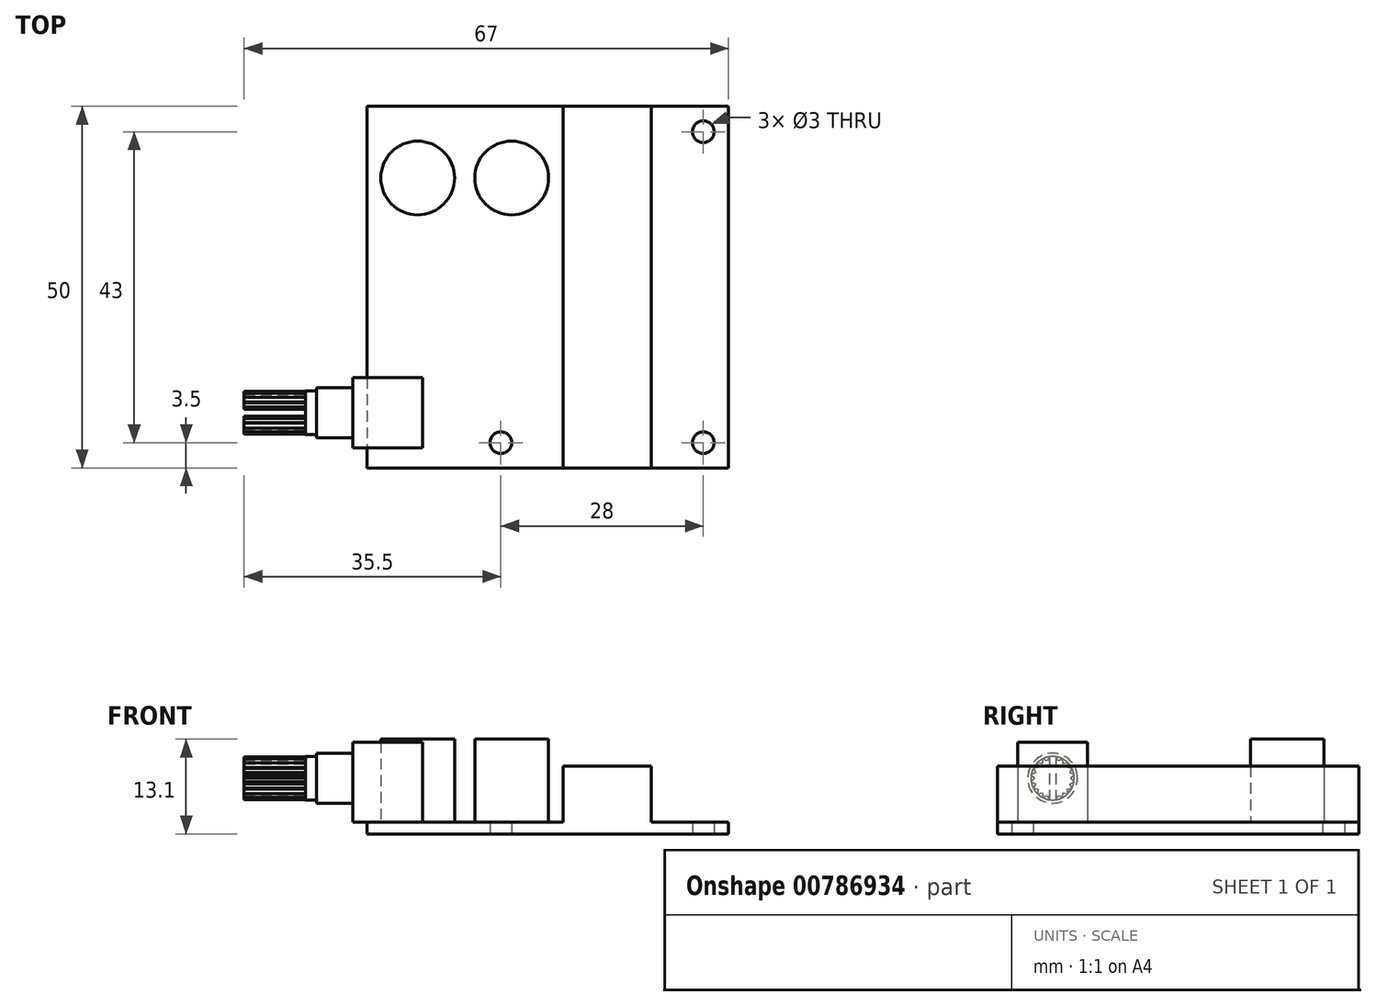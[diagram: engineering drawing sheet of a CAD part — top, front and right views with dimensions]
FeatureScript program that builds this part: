
annotation { "Feature Type Name" : "Feature", "Feature Type Description" : "" }
export const myFeature = defineFeature(function(context is Context, id is Id, definition is map)
    precondition{}
    {
        {
            var Q0;
            Q0=qCreatedBy(makeId("Top.planeOp"),FACE);
            var sketch = newSketch(context, id + "F0", { "sketchPlane" : qUnion([Q0])});
            skLineSegment(sketch, "E0.bottom", {"start": v(-25, 25) * mm, "end": v(25, 25) * mm});
            skLineSegment(sketch, "E0.top", {"start": v(-25, -25) * mm, "end": v(25, -25) * mm});
            skLineSegment(sketch, "E0.left", {"start": v(-25, 25) * mm, "end": v(-25, -25) * mm});
            skLineSegment(sketch, "E0.right", {"start": v(25, 25) * mm, "end": v(25, -25) * mm});
            skCircle(sketch, "E1", {"center": v(21.5, 21.5) * mm, "radius": 1.5 * mm});
            skCircle(sketch, "E2", {"center": v(21.5, -21.5) * mm, "radius": 1.5 * mm});
            skCircle(sketch, "E3", {"center": v(-6.5, -21.5) * mm, "radius": 1.5 * mm});
            skSolve(sketch);
        }
        {
            var Q0;
            Q0=makeQuery(id+"F0.imprint","IMPRINT",FACE,{"disambiguationData":[TD([[makeQuery(id+"F0.imprint","IMPRINT",EDGE,{"derivedFrom":sQuery(id+"F0.wireOp",EDGE,"E0.bottom")}),-1.0]])]});
            extrude(context, id + "F1", {"entities" : qUnion([Q0]), "depth" : 1.6 * mm, "offsetDistance" : 25 * mm});
        }
        {
            var Q0;
            Q0=makeQuery(id+"F1.opExtrude","CAP_FACE",FACE,{"disambiguationData":[OSD([sQuery(id+"F0.wireOp",EDGE,"E0.bottom"),sQuery(id+"F0.wireOp",EDGE,"E0.top"),sQuery(id+"F0.wireOp",EDGE,"E0.left"),sQuery(id+"F0.wireOp",EDGE,"E0.right"),sQuery(id+"F0.wireOp",EDGE,"E1"),sQuery(id+"F0.wireOp",EDGE,"E2"),sQuery(id+"F0.wireOp",EDGE,"E3")])],"isStart":false});
            var sketch = newSketch(context, id + "F2", { "sketchPlane" : qUnion([Q0])});
            skLineSegment(sketch, "E4.bottom", {"start": v(2.1, 25) * mm, "end": v(14.3, 25) * mm});
            skLineSegment(sketch, "E4.top", {"start": v(2.1, -25) * mm, "end": v(14.3, -25) * mm});
            skLineSegment(sketch, "E4.left", {"start": v(2.1, 25) * mm, "end": v(2.1, -25) * mm});
            skLineSegment(sketch, "E4.right", {"start": v(14.3, 25) * mm, "end": v(14.3, -25) * mm});
            skSolve(sketch);
        }
        {
            var Q0;
            Q0 = qSketchRegion(id + "F2", true);
            extrude(context, id + "F3", {"entities" : qUnion([Q0]), "operationType" : NewBodyOperationType.ADD, "depth" : (9.37 - 1.6) * mm, "offsetDistance" : 25 * mm});
        }
        {
            var Q0;
            {var subQ0=sQuery(id+"F0.wireOp",EDGE,"E0.left");var subQ1=sQuery(id+"F0.wireOp",EDGE,"E3");var subQ2=sQuery(id+"F0.wireOp",EDGE,"E0.top");var subQ3=sQuery(id+"F0.wireOp",EDGE,"E0.bottom");Q0=makeQuery(id+"F3.boolean.opBoolean","SPLIT",FACE,{"disambiguationData":[TD([makeQuery(id+"F1.opExtrude","SWEPT_FACE",FACE,{"disambiguationData":[OSD([subQ0])]})])],"derivedFrom":makeQuery(id+"F1.opExtrude","CAP_FACE",FACE,{"disambiguationData":[OSD([subQ3,subQ2,subQ0,sQuery(id+"F0.wireOp",EDGE,"E0.right"),sQuery(id+"F0.wireOp",EDGE,"E1"),sQuery(id+"F0.wireOp",EDGE,"E2"),subQ1])],"isStart":false})});}
            var sketch = newSketch(context, id + "F4", { "sketchPlane" : qUnion([Q0])});
            skCircle(sketch, "E5", {"center": v(-18, 15.1) * mm, "radius": 5.1 * mm});
            skCircle(sketch, "E6", {"center": v(-5, 15.1) * mm, "radius": 5.1 * mm});
            skSolve(sketch);
        }
        {
            var Q0;
            Q0 = qSketchRegion(id + "F4", true);
            extrude(context, id + "F5", {"entities" : qUnion([Q0]), "operationType" : NewBodyOperationType.ADD, "depth" : (13.1 - 1.6) * mm, "offsetDistance" : 25 * mm});
        }
        {
            var Q0;
            {var subQ0=sQuery(id+"F0.wireOp",EDGE,"E0.left");var subQ1=sQuery(id+"F0.wireOp",EDGE,"E3");var subQ2=sQuery(id+"F0.wireOp",EDGE,"E0.top");var subQ3=sQuery(id+"F0.wireOp",EDGE,"E0.bottom");Q0=makeQuery(id+"F3.boolean.opBoolean","SPLIT",FACE,{"disambiguationData":[TD([makeQuery(id+"F1.opExtrude","SWEPT_FACE",FACE,{"disambiguationData":[OSD([subQ0])]})])],"derivedFrom":makeQuery(id+"F1.opExtrude","CAP_FACE",FACE,{"disambiguationData":[OSD([subQ3,subQ2,subQ0,sQuery(id+"F0.wireOp",EDGE,"E0.right"),sQuery(id+"F0.wireOp",EDGE,"E1"),sQuery(id+"F0.wireOp",EDGE,"E2"),subQ1])],"isStart":false})});}
            var sketch = newSketch(context, id + "F6", { "sketchPlane" : qUnion([Q0])});
            skLineSegment(sketch, "E7.bottom", {"start": v(-27, -12.5) * mm, "end": v(-17.3, -12.5) * mm});
            skLineSegment(sketch, "E7.top", {"start": v(-27, -22.2) * mm, "end": v(-17.3, -22.2) * mm});
            skLineSegment(sketch, "E7.left", {"start": v(-27, -12.5) * mm, "end": v(-27, -22.2) * mm});
            skLineSegment(sketch, "E7.right", {"start": v(-17.3, -12.5) * mm, "end": v(-17.3, -22.2) * mm});
            skSolve(sketch);
        }
        {
            var Q0;
            Q0 = qSketchRegion(id + "F6", true);
            extrude(context, id + "F7", {"entities" : qUnion([Q0]), "operationType" : NewBodyOperationType.ADD, "depth" : 11.1 * mm, "offsetDistance" : 25 * mm});
        }
        {
            var Q0;
            Q0=makeQuery(id+"F7.opExtrude","SWEPT_FACE",FACE,{"disambiguationData":[OSD([sQuery(id+"F6.wireOp",EDGE,"E7.left")])]});
            var sketch = newSketch(context, id + "F8", { "sketchPlane" : qUnion([Q0])});
            skCircle(sketch, "E8", {"center": v(17.35, 7.7) * mm, "radius": 3.45 * mm});
            skSolve(sketch);
        }
        {
            var Q0;
            Q0 = qSketchRegion(id + "F8", true);
            extrude(context, id + "F9", {"entities" : qUnion([Q0]), "operationType" : NewBodyOperationType.ADD, "depth" : 5 * mm, "offsetDistance" : 25 * mm});
        }
        {
            var Q0;
            Q0=makeQuery(id+"F9.opExtrude","CAP_FACE",FACE,{"disambiguationData":[OSD([sQuery(id+"F8.wireOp",EDGE,"E8")])],"isStart":false});
            var sketch = newSketch(context, id + "F10", { "sketchPlane" : qUnion([Q0])});
            skCircle(sketch, "E9", {"center": v(17.35, 7.7) * mm, "radius": 3 * mm});
            skSolve(sketch);
        }
        {
            var Q0;
            Q0 = qSketchRegion(id + "F10", true);
            extrude(context, id + "F11", {"entities" : qUnion([Q0]), "operationType" : NewBodyOperationType.ADD, "depth" : 1.5 * mm, "offsetDistance" : 25 * mm});
        }
        {
            var Q0;
            Q0=makeQuery(id+"F11.opExtrude","CAP_FACE",FACE,{"disambiguationData":[OSD([sQuery(id+"F10.wireOp",EDGE,"E9")])],"isStart":false});
            var sketch = newSketch(context, id + "F12", { "sketchPlane" : qUnion([Q0])});
            skPoint(sketch, "E10", {"position": v(17.35, 7.7) * mm});
            skLineSegment(sketch, "E11", {"start": v(17.35, 7.7) * mm, "end": v(17.35, 10.7) * mm, "construction": true});
            skLineSegment(sketch, "E12", {"start": v(16.88, 10.66) * mm, "end": v(17.35, 10.2) * mm});
            skLineSegment(sketch, "E13", {"start": v(17.35, 10.2) * mm, "end": v(17.82, 10.66) * mm});
            skLineSegment(sketch, "E14", {"start": v(17.35, 7.7) * mm, "end": v(16.88, 10.66) * mm, "construction": true});
            skLineSegment(sketch, "E15", {"start": v(17.35, 7.7) * mm, "end": v(17.82, 10.66) * mm, "construction": true});
            skLineSegment(sketch, "E16.1.0", {"start": v(15.99, 10.37) * mm, "end": v(16.58, 10.08) * mm});
            skLineSegment(sketch, "E16.1.1", {"start": v(16.58, 10.08) * mm, "end": v(16.88, 10.66) * mm});
            skLineSegment(sketch, "E16.2.0", {"start": v(15.23, 9.82) * mm, "end": v(15.88, 9.72) * mm});
            skLineSegment(sketch, "E16.2.1", {"start": v(15.88, 9.72) * mm, "end": v(15.99, 10.37) * mm});
            skLineSegment(sketch, "E17.1.3.0", {"start": v(14.68, 9.06) * mm, "end": v(15.33, 9.17) * mm});
            skLineSegment(sketch, "E17.3.3.0", {"start": v(15.33, 9.17) * mm, "end": v(15.23, 9.82) * mm});
            skLineSegment(sketch, "E17.1.4.0", {"start": v(14.39, 8.17) * mm, "end": v(14.97, 8.47) * mm});
            skLineSegment(sketch, "E17.3.4.0", {"start": v(14.97, 8.47) * mm, "end": v(14.68, 9.06) * mm});
            skLineSegment(sketch, "E17.1.5.0", {"start": v(14.39, 7.23) * mm, "end": v(14.85, 7.7) * mm});
            skLineSegment(sketch, "E17.3.5.0", {"start": v(14.85, 7.7) * mm, "end": v(14.39, 8.17) * mm});
            skLineSegment(sketch, "E17.1.6.0", {"start": v(14.68, 6.34) * mm, "end": v(14.97, 6.93) * mm});
            skLineSegment(sketch, "E17.3.6.0", {"start": v(14.97, 6.93) * mm, "end": v(14.39, 7.23) * mm});
            skLineSegment(sketch, "E17.1.7.0", {"start": v(15.23, 5.58) * mm, "end": v(15.33, 6.23) * mm});
            skLineSegment(sketch, "E17.3.7.0", {"start": v(15.33, 6.23) * mm, "end": v(14.68, 6.34) * mm});
            skLineSegment(sketch, "E17.1.8.0", {"start": v(15.99, 5.03) * mm, "end": v(15.88, 5.68) * mm});
            skLineSegment(sketch, "E17.3.8.0", {"start": v(15.88, 5.68) * mm, "end": v(15.23, 5.58) * mm});
            skLineSegment(sketch, "E17.1.9.0", {"start": v(16.88, 4.74) * mm, "end": v(16.58, 5.32) * mm});
            skLineSegment(sketch, "E17.3.9.0", {"start": v(16.58, 5.32) * mm, "end": v(15.99, 5.03) * mm});
            skLineSegment(sketch, "E17.1.10.0", {"start": v(17.82, 4.74) * mm, "end": v(17.35, 5.2) * mm});
            skLineSegment(sketch, "E17.3.10.0", {"start": v(17.35, 5.2) * mm, "end": v(16.88, 4.74) * mm});
            skLineSegment(sketch, "E17.1.11.0", {"start": v(18.71, 5.03) * mm, "end": v(18.12, 5.32) * mm});
            skLineSegment(sketch, "E17.3.11.0", {"start": v(18.12, 5.32) * mm, "end": v(17.82, 4.74) * mm});
            skLineSegment(sketch, "E18.1.12.0", {"start": v(19.47, 5.58) * mm, "end": v(18.82, 5.68) * mm});
            skLineSegment(sketch, "E18.3.12.0", {"start": v(18.82, 5.68) * mm, "end": v(18.71, 5.03) * mm});
            skLineSegment(sketch, "E18.1.13.0", {"start": v(20.02, 6.34) * mm, "end": v(19.37, 6.23) * mm});
            skLineSegment(sketch, "E18.3.13.0", {"start": v(19.37, 6.23) * mm, "end": v(19.47, 5.58) * mm});
            skLineSegment(sketch, "E18.1.14.0", {"start": v(20.31, 7.23) * mm, "end": v(19.73, 6.93) * mm});
            skLineSegment(sketch, "E18.3.14.0", {"start": v(19.73, 6.93) * mm, "end": v(20.02, 6.34) * mm});
            skLineSegment(sketch, "E18.1.15.0", {"start": v(20.31, 8.17) * mm, "end": v(19.85, 7.7) * mm});
            skLineSegment(sketch, "E18.3.15.0", {"start": v(19.85, 7.7) * mm, "end": v(20.31, 7.23) * mm});
            skLineSegment(sketch, "E18.1.16.0", {"start": v(20.02, 9.06) * mm, "end": v(19.73, 8.47) * mm});
            skLineSegment(sketch, "E18.3.16.0", {"start": v(19.73, 8.47) * mm, "end": v(20.31, 8.17) * mm});
            skLineSegment(sketch, "E18.1.17.0", {"start": v(19.47, 9.82) * mm, "end": v(19.37, 9.17) * mm});
            skLineSegment(sketch, "E18.3.17.0", {"start": v(19.37, 9.17) * mm, "end": v(20.02, 9.06) * mm});
            skLineSegment(sketch, "E18.1.18.0", {"start": v(18.71, 10.37) * mm, "end": v(18.82, 9.72) * mm});
            skLineSegment(sketch, "E18.3.18.0", {"start": v(18.82, 9.72) * mm, "end": v(19.47, 9.82) * mm});
            skLineSegment(sketch, "E18.1.19.0", {"start": v(17.82, 10.66) * mm, "end": v(18.12, 10.08) * mm});
            skLineSegment(sketch, "E18.3.19.0", {"start": v(18.12, 10.08) * mm, "end": v(18.71, 10.37) * mm});
            skLineSegment(sketch, "E19", {"start": v(16.88, 10.66) * mm, "end": v(16.88, 4.74) * mm});
            skLineSegment(sketch, "E20", {"start": v(17.82, 10.66) * mm, "end": v(17.82, 4.74) * mm});
            skSolve(sketch);
        }
        {
            var Q0;
            Q0=makeQuery(id+"F12.imprint","IMPRINT",FACE,{"disambiguationData":[TD([[makeQuery(id+"F12.imprint","IMPRINT",EDGE,{"derivedFrom":sQuery(id+"F12.wireOp",EDGE,"E16.1.0")}),-1.0]])]});
            var Q1;
            Q1=makeQuery(id+"F12.imprint","IMPRINT",FACE,{"disambiguationData":[TD([[makeQuery(id+"F12.imprint","IMPRINT",EDGE,{"derivedFrom":sQuery(id+"F12.wireOp",EDGE,"E17.1.11.0")}),-1.0]])]});
            extrude(context, id + "F13", {"entities" : qUnion([Q0, Q1]), "operationType" : NewBodyOperationType.ADD, "depth" : 8.5 * mm, "offsetDistance" : 25 * mm});
        }
    });
